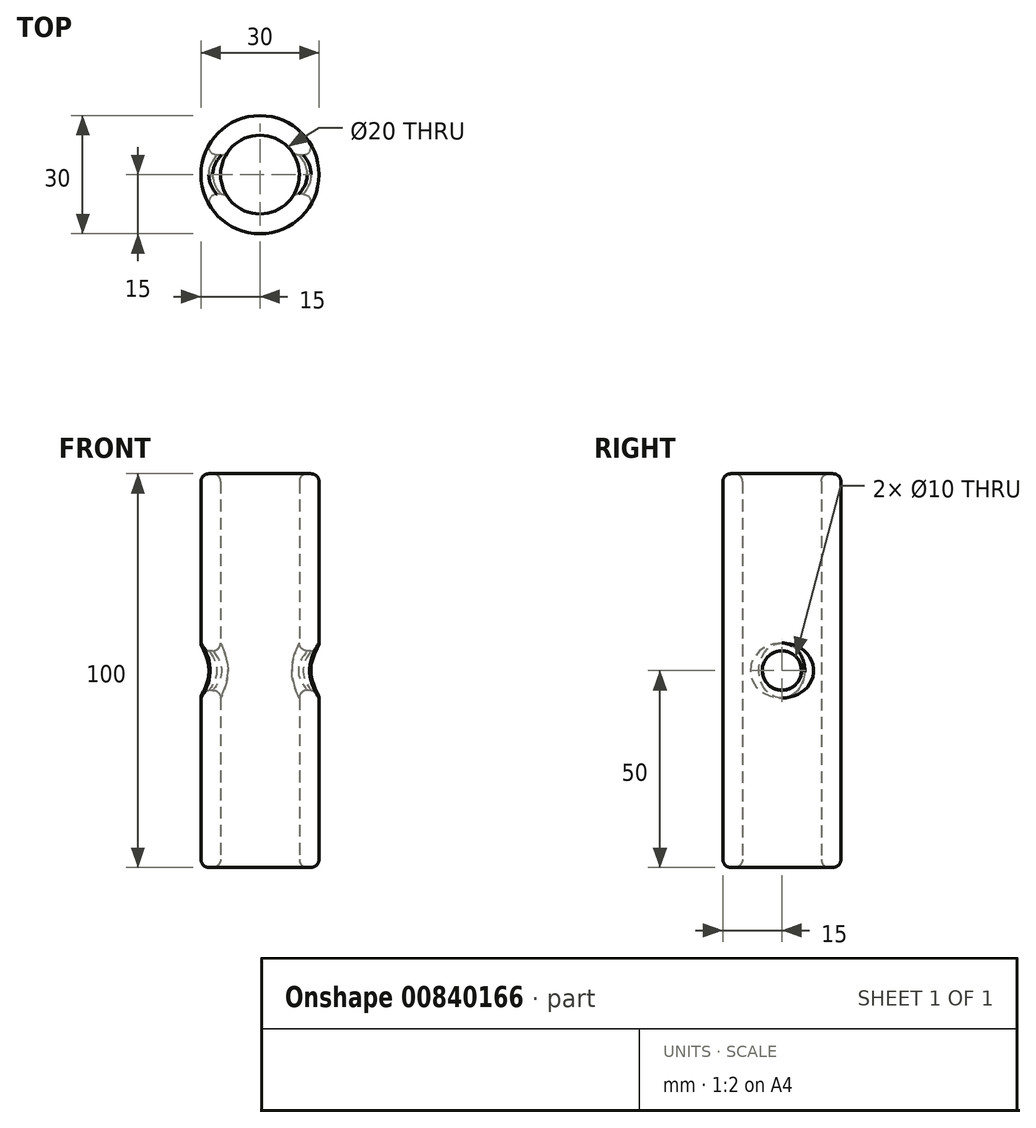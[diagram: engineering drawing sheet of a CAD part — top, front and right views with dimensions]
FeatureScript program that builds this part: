
annotation { "Feature Type Name" : "Feature", "Feature Type Description" : "" }
export const myFeature = defineFeature(function(context is Context, id is Id, definition is map)
    precondition{}
    {
        {
            var Q0;
            Q0=qCreatedBy(makeId("Top.planeOp"),FACE);
            var sketch = newSketch(context, id + "F0", { "sketchPlane" : qUnion([Q0])});
            skCircle(sketch, "E0", {"center": v(0, 0) * mm, "radius": 10 * mm});
            skCircle(sketch, "E1", {"center": v(0, 0) * mm, "radius": 15 * mm});
            skSolve(sketch);
        }
        {
            var Q0;
            Q0 = qSketchRegion(id + "F0", true);
            extrude(context, id + "F1", {"entities" : qUnion([Q0]), "endBound" : BoundingType.SYMMETRIC, "depth" : 100 * mm, "offsetDistance" : 25 * mm});
        }
        {
            var Q0;
            Q0=qCreatedBy(makeId("Right.planeOp"),FACE);
            var sketch = newSketch(context, id + "F2", { "sketchPlane" : qUnion([Q0])});
            skCircle(sketch, "E2", {"center": v(0, 0) * mm, "radius": 5 * mm});
            skSolve(sketch);
        }
        {
            var Q0;
            Q0 = qSketchRegion(id + "F2", true);
            extrude(context, id + "F3", {"entities" : qUnion([Q0]), "operationType" : NewBodyOperationType.REMOVE, "endBound" : BoundingType.SYMMETRIC, "depth" : 40 * mm, "offsetDistance" : 25 * mm});
        }
        {
            var Q0;
            Q0=makeQuery(id+"F1.opExtrude","CAP_FACE",FACE,{"disambiguationData":[OSD([sQuery(id+"F0.wireOp",EDGE,"E0"),sQuery(id+"F0.wireOp",EDGE,"E1")])],"isStart":true});
            fillet(context, id + "F4", {"entities" : qUnion([Q0]), "radius" : 2 * mm, "tangentPropagation" : true, "allowEdgeOverflow" : false});
        }
        {
            var Q0;
            Q0=makeQuery(id+"F1.opExtrude","CAP_FACE",FACE,{"disambiguationData":[OSD([sQuery(id+"F0.wireOp",EDGE,"E0"),sQuery(id+"F0.wireOp",EDGE,"E1")])],"isStart":false});
            fillet(context, id + "F5", {"entities" : qUnion([Q0]), "radius" : 2 * mm, "tangentPropagation" : true, "allowEdgeOverflow" : false});
        }
        {
            var Q0;
            Q0=makeQuery(id+"F3.boolean.opBoolean","COPY",FACE,{"disambiguationData":[OD(1.0)],"derivedFrom":makeQuery(id+"F3.opExtrude","SWEPT_FACE",FACE,{"disambiguationData":[OSD([sQuery(id+"F2.wireOp",EDGE,"E2")])]})});
            fillet(context, id + "F6", {"entities" : qUnion([Q0]), "radius" : 2 * mm, "tangentPropagation" : true, "allowEdgeOverflow" : false});
        }
        {
            var Q0;
            Q0=makeQuery(id+"F3.boolean.opBoolean","COPY",FACE,{"disambiguationData":[OD(0.0)],"derivedFrom":makeQuery(id+"F3.opExtrude","SWEPT_FACE",FACE,{"disambiguationData":[OSD([sQuery(id+"F2.wireOp",EDGE,"E2")])]})});
            fillet(context, id + "F7", {"entities" : qUnion([Q0]), "radius" : 2 * mm, "tangentPropagation" : true, "allowEdgeOverflow" : false});
        }
    });
